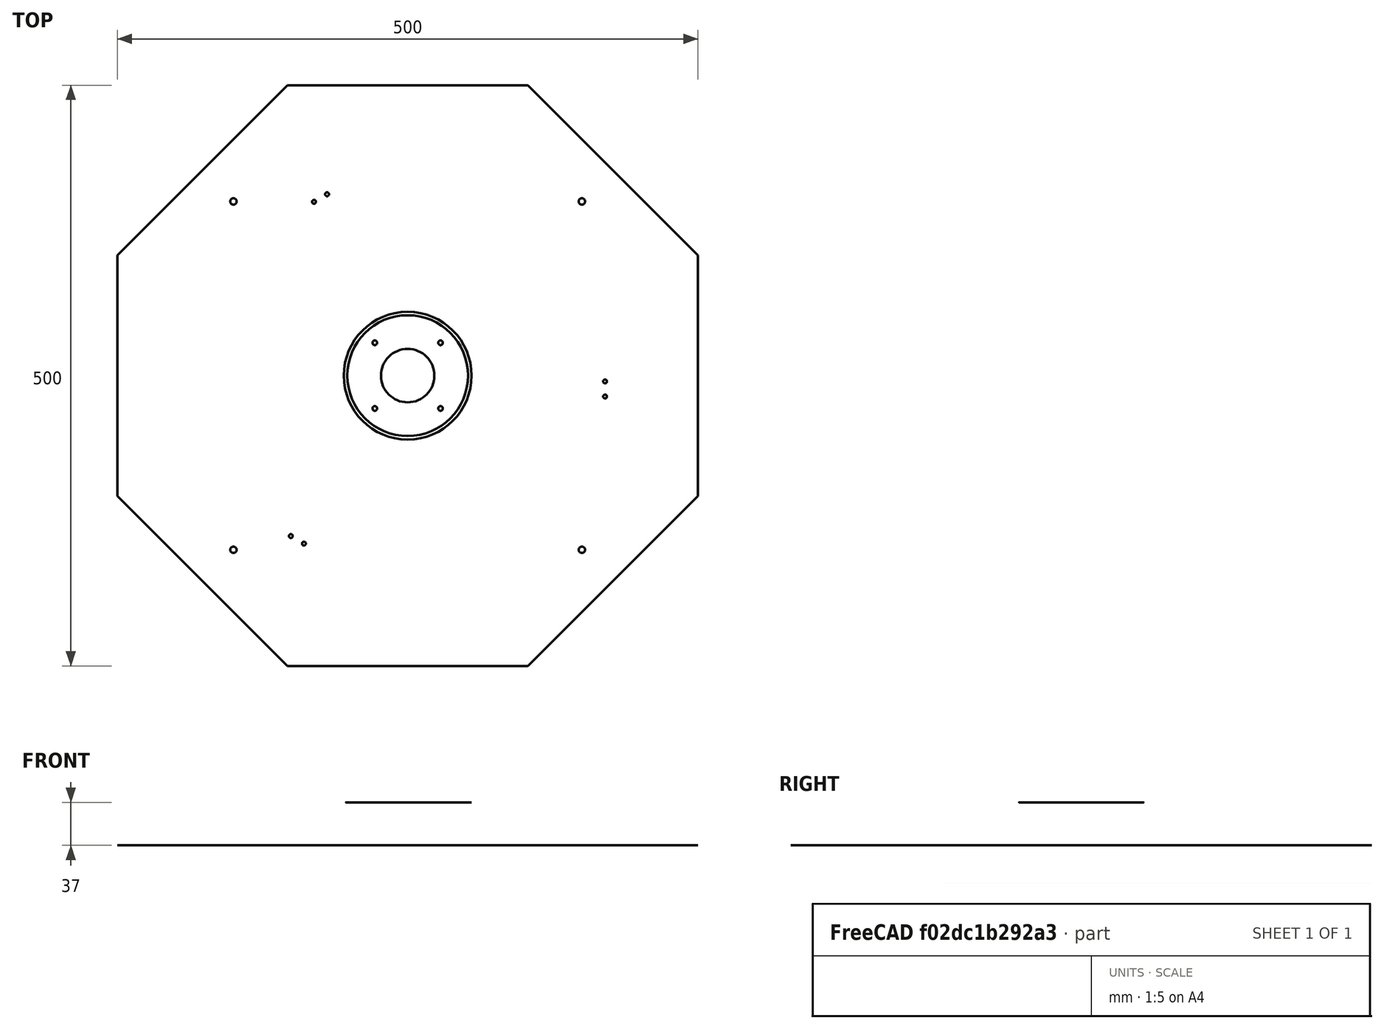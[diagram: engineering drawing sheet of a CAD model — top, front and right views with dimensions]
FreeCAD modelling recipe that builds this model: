
FCSTD DOCUMENT  (FreeCAD 0.19R24276 (Git))
Label: Baugruppe_Lampe_4er
License: All rights reserved
LicenseURL: http://en.wikipedia.org/wiki/All_rights_reserved
objects: Part::FeaturePython×25, App::Link×10, App::FeaturePython×5
note: 24 computed .brp shape members not serialized (recipe doc carries the construction recipe); baked Part::Feature solids carry a one-line shape summary decoded from their .brp
EXTERNAL_REF file=Metalicht_v2.FCStd obj=Body
EXTERNAL_REF file=Trichter.FCStd obj=Body
EXTERNAL_REF file=Birne_mit_Fassung.FCStd obj=Body
EXTERNAL_REF file=Wago_5x_flach.FCStd obj=Part__Feature

FEATURE [App::Link] Link  label="Body"
  LinkedObject = -> <external Metalicht_v2.FCStd>#Body
FEATURE [App::Link] Link001  label="Body001"
  LinkPlacement = pos=(0,0,1) rot=(0,0,1;0rad)
  LinkedObject = -> <external Trichter.FCStd>#Body
  Placement = pos=(0,0,1) rot=(0,0,1;0rad)
FEATURE [App::Link] Link002  label="Body002"
  LinkPlacement = pos=(164.77,44.4951,33.009) rot=(-0.043599,0.030528,-0.998583;4.36199rad)
  LinkedObject = -> <external Birne_mit_Fassung.FCStd>#Body
  Placement = pos=(164.77,44.4951,33.009) rot=(-0.043599,0.030528,-0.998583;4.36199rad)
FEATURE [App::Link] Link003  label="Body003"
  LinkPlacement = pos=(-44.668,164.613,33.009) rot=(0.043618,0.007691,0.999019;3.49032rad)
  LinkedObject = -> <external Birne_mit_Fassung.FCStd>#Body
  Placement = pos=(-44.668,164.613,33.009) rot=(0.043618,0.007691,0.999019;3.49032rad)
FEATURE [App::Link] Link004  label="Body004"
  LinkPlacement = pos=(44.4121,-164.782,33.0089) rot=(0.042343,-0.240138,0.969815;0.359701rad)
  LinkedObject = -> <external Birne_mit_Fassung.FCStd>#Body
  Placement = pos=(44.4121,-164.782,33.0089) rot=(0.042343,-0.240138,0.969815;0.359701rad)
FEATURE [App::Link] Link005  label="Wago_5x_flach"
  LinkPlacement = pos=(-69.5826,-37.87,-17.9525) rot=(0.57735,0.57735,-0.57735;4.18879rad)
  LinkedObject = -> <external Wago_5x_flach.FCStd>#Part__Feature
  Placement = pos=(-69.5826,-37.87,-17.9525) rot=(0.57735,0.57735,-0.57735;4.18879rad)
FEATURE [App::Link] Link006  label="Wago_5x_flach001"
  LinkPlacement = pos=(-69.5,59.5001,-18) rot=(0.57735,0.57735,-0.57735;4.18879rad)
  LinkedObject = -> <external Wago_5x_flach.FCStd>#Part__Feature
  Placement = pos=(-69.5,59.5001,-18) rot=(0.57735,0.57735,-0.57735;4.18879rad)
FEATURE [App::Link] Link007  label="Body005"
  LinkPlacement = pos=(-164.611,-44.4205,33.0759) rot=(-0.043535,-0.062174,-0.997115;1.22445rad)
  LinkedObject = -> <external Birne_mit_Fassung.FCStd>#Body
  Placement = pos=(-164.611,-44.4205,33.0759) rot=(-0.043535,-0.062174,-0.997115;1.22445rad)
FEATURE [App::Link] Link008  label="Wago_5x_flach002"
  LinkPlacement = pos=(69.5,-59.5001,-18) rot=(0.57735,-0.57735,0.57735;4.18879rad)
  LinkedObject = -> <external Wago_5x_flach.FCStd>#Part__Feature
  Placement = pos=(69.5,-59.5001,-18) rot=(0.57735,-0.57735,0.57735;4.18879rad)
FEATURE [App::Link] Link009  label="Wago_5x_flach003"
  LinkPlacement = pos=(69.546,37.646,-17.9) rot=(-0.57735,0.57735,-0.57735;2.0944rad)
  LinkedObject = -> <external Wago_5x_flach.FCStd>#Part__Feature
  Placement = pos=(69.546,37.646,-17.9) rot=(-0.57735,0.57735,-0.57735;2.0944rad)
FEATURE [Part::FeaturePython] Parts  # WARN: FeaturePython — macro-defined, semantics opaque (R4)
  Group = -> [Link,Link001,Link002,Link003,Link004,Link005,Link006,Link007,Link008,Link009]
  GroupMode = 0
FEATURE [Part::FeaturePython] Assembly  # WARN: FeaturePython — macro-defined, semantics opaque (R4)
  AutoRelax = true
  BuildShape = 0
  Freeze = false
  Group = -> [Constraints,Elements,Parts]
  Verbose = false
  _SolverType = 1
  _Version = 1
FEATURE [App::FeaturePython] Constraints  # WARN: FeaturePython — macro-defined, semantics opaque (R4)
  Group = -> [Constraint]
  _Version = 1
FEATURE [App::FeaturePython] Elements  # WARN: FeaturePython — macro-defined, semantics opaque (R4)
  Group = -> [_Element,_Element001,_Element002,_Element003,_Element004,_Element005,_Element006,_Element007,_Element008,_Element009,_Element010,_Element011,_Element012,_Element013,_Element014,_Element015,_Element016,_Element017,_Element018,_Element019,_Element020,_Element021,_Element022]
FEATURE [App::FeaturePython] Constraint  label="Locked"  # WARN: FeaturePython — macro-defined, semantics opaque (R4)
  Disabled = false
  Group = -> [ElementLink,ElementLink001]
  _ConstraintType = 0
  _Parent = -> Constraints
FEATURE [App::FeaturePython] ElementLink  label="_Element"  # link proxy (typed FeaturePython)
  LinkTransform = true
  LinkedObject = -> _Element
  _Parent = -> Constraint
FEATURE [Part::FeaturePython] _Element  # link proxy (typed FeaturePython)
  Detach = false
  LinkTransform = true
  LinkedObject = -> Link [PolarPattern.Face5]
  _Parent = -> Elements
FEATURE [App::FeaturePython] ElementLink001  label="_Element001"  # link proxy (typed FeaturePython)
  LinkTransform = true
  LinkedObject = -> _Element001
  _Parent = -> Constraint
FEATURE [Part::FeaturePython] _Element001  # link proxy (typed FeaturePython)
  Detach = false
  LinkTransform = true
  LinkedObject = -> Link001 [Revolution.Face2]
  _Parent = -> Elements
FEATURE [Part::FeaturePython] _Element002  # link proxy (typed FeaturePython)
  Detach = false
  LinkTransform = true
  LinkedObject = -> Link [PolarPattern.Edge37]
  _Parent = -> Elements
FEATURE [Part::FeaturePython] _Element003  # link proxy (typed FeaturePython)
  Detach = false
  LinkTransform = true
  LinkedObject = -> Link003 [Hole.Edge39]
  _Parent = -> Elements
FEATURE [Part::FeaturePython] _Element004  # link proxy (typed FeaturePython)
  Detach = false
  LinkTransform = true
  LinkedObject = -> Link [PolarPattern.Edge35]
  _Parent = -> Elements
FEATURE [Part::FeaturePython] _Element005  # link proxy (typed FeaturePython)
  Detach = false
  LinkTransform = true
  LinkedObject = -> Link003 [Hole.Edge38]
  _Parent = -> Elements
FEATURE [Part::FeaturePython] _Element006  # link proxy (typed FeaturePython)
  Detach = false
  LinkTransform = true
  LinkedObject = -> Link004 [Hole.Edge38]
  _Parent = -> Elements
FEATURE [Part::FeaturePython] _Element007  # link proxy (typed FeaturePython)
  Detach = false
  LinkTransform = true
  LinkedObject = -> Link [PolarPattern.Edge29]
  _Parent = -> Elements
FEATURE [Part::FeaturePython] _Element008  # link proxy (typed FeaturePython)
  Detach = false
  LinkTransform = true
  LinkedObject = -> Link [PolarPattern.Edge30]
  _Parent = -> Elements
FEATURE [Part::FeaturePython] _Element009  # link proxy (typed FeaturePython)
  Detach = false
  LinkTransform = true
  LinkedObject = -> Link004 [Hole.Edge39]
  _Parent = -> Elements
FEATURE [Part::FeaturePython] _Element010  # link proxy (typed FeaturePython)
  Detach = false
  LinkTransform = true
  LinkedObject = -> Link002 [Hole.Edge38]
  _Parent = -> Elements
FEATURE [Part::FeaturePython] _Element011  # link proxy (typed FeaturePython)
  Detach = false
  LinkTransform = true
  LinkedObject = -> Link [PolarPattern.Edge33]
  _Parent = -> Elements
FEATURE [Part::FeaturePython] _Element012  # link proxy (typed FeaturePython)
  Detach = false
  LinkTransform = true
  LinkedObject = -> Link [PolarPattern.Edge32]
  _Parent = -> Elements
FEATURE [Part::FeaturePython] _Element013  # link proxy (typed FeaturePython)
  Detach = false
  LinkTransform = true
  LinkedObject = -> Link002 [Hole.Edge39]
  _Parent = -> Elements
FEATURE [Part::FeaturePython] _Element014  # link proxy (typed FeaturePython)
  Detach = false
  LinkTransform = true
  LinkedObject = -> Link [PolarPattern.Edge36]
  _Parent = -> Elements
FEATURE [Part::FeaturePython] _Element015  # link proxy (typed FeaturePython)
  Detach = false
  LinkTransform = true
  LinkedObject = -> Link [PolarPattern.Edge34]
  _Parent = -> Elements
FEATURE [Part::FeaturePython] _Element016  # link proxy (typed FeaturePython)
  Detach = false
  LinkTransform = true
  LinkedObject = -> Link [Pocket002.Edge64]
  _Parent = -> Elements
FEATURE [Part::FeaturePython] _Element017  # link proxy (typed FeaturePython)
  Detach = false
  LinkTransform = true
  LinkedObject = -> Link [Pocket002.Edge63]
  _Parent = -> Elements
FEATURE [Part::FeaturePython] _Element018  # link proxy (typed FeaturePython)
  Detach = false
  LinkTransform = true
  LinkedObject = -> Link [Pocket002.Edge100]
  _Parent = -> Elements
FEATURE [Part::FeaturePython] _Element019  # link proxy (typed FeaturePython)
  Detach = false
  LinkTransform = true
  LinkedObject = -> Link [Pocket002.Edge99]
  _Parent = -> Elements
FEATURE [Part::FeaturePython] _Element020  # link proxy (typed FeaturePython)
  Detach = false
  LinkTransform = true
  LinkedObject = -> Link [Pocket002.Edge86]
  _Parent = -> Elements
FEATURE [Part::FeaturePython] _Element021  # link proxy (typed FeaturePython)
  Detach = false
  LinkTransform = true
  LinkedObject = -> Link [Pocket002.Edge88]
  _Parent = -> Elements
FEATURE [Part::FeaturePython] _Element022  # link proxy (typed FeaturePython)
  Detach = false
  LinkTransform = true
  LinkedObject = -> Link [Pocket002.Edge87]
  _Parent = -> Elements

RESOLVED EXTERNAL PARTS (link-assembly join: the EXTERNAL_REF files above that resolve inside this repo's crawl, each included once):
---- part Birne_mit_Fassung.FCStd = doc fcstd_91edc3af70b6 ----
FCSTD DOCUMENT  (FreeCAD 0.19R24276 (Git))
Label: Birne_mit_Fassung
License: All rights reserved
LicenseURL: http://en.wikipedia.org/wiki/All_rights_reserved
objects: Sketcher::SketchObject×3, PartDesign::Revolution×1, PartDesign::Pad×1, PartDesign::Fillet×1, PartDesign::Hole×1, PartDesign::Body×1
note: 12 computed .brp shape members not serialized (recipe doc carries the construction recipe); baked Part::Feature solids carry a one-line shape summary decoded from their .brp

FEATURE [Sketcher::SketchObject] Sketch
  FullyConstrained = true
  MapMode = 5
  Placement = pos=(0,0,0) rot=(1,0,0;1.5708rad)
  Support = -> [XZ_Plane]
  sketch-geometry (8):
    g0: LineSegment StartX=0 StartY=0 StartZ=0 EndX=0 EndY=17.5 EndZ=0
    g1: LineSegment StartX=0 StartY=17.5 StartZ=0 EndX=36 EndY=20 EndZ=0
    g2: LineSegment StartX=36 StartY=20 StartZ=0 EndX=36 EndY=21 EndZ=0
    g3: LineSegment StartX=36 StartY=21 StartZ=0 EndX=48 EndY=21 EndZ=0
    g4: LineSegment StartX=48 StartY=21 StartZ=0 EndX=48 EndY=17 EndZ=0
    g5: LineSegment StartX=48 StartY=17 StartZ=0 EndX=87 EndY=21.4243 EndZ=0
    g6: ArcOfCircle CenterX=108 CenterY=0 CenterZ=0 NormalX=0 NormalY=0 NormalZ=1 AngleXU=0 Radius=30 StartAngle=0 EndAngle=2.34619
    g7: LineSegment StartX=138 StartY=0 StartZ=0 EndX=0 EndY=0 EndZ=0
  constraints (24):
    c: Coincident(g-1,g0)
    c: PointOnObject(g0,g-2)
    c: Coincident(g0,g1)
    c: Coincident(g1,g2)
    c: Vertical(g2)
    c: Coincident(g2,g3)
    c: Horizontal(g3)
    c: Coincident(g3,g4)
    c: Vertical(g4)
    c: Coincident(g4,g5)
    c: PointOnObject(g6,g-1)
    c: Coincident(g6,g5)
    c: PointOnObject(g6,g-1)
    c: Coincident(g7,g6)
    c: Coincident(g7,g0)
    c: DistanceX(g0,g3) = 48
    c: Radius(g6) = 30
    c: DistanceX(g4,g6) = 90
    c: DistanceX(g3,g3) = 12
    c: DistanceX(g4,g5) = 39
    c: DistanceY(g0,g0) = 17.5
    c: DistanceY(g0,g3) = 21
    c: DistanceY(g2,g2) = 1
    c: DistanceY(g0,g4) = 17
FEATURE [PartDesign::Revolution] Revolution
  Angle = 360
  Axis = (1,0,0)
  Base = (0,0,0)
  Placement = pos=(0,0,0) rot=(1,0,0;1.5708rad)
  Profile = -> Sketch
  ReferenceAxis = -> Sketch [H_Axis]
FEATURE [Sketcher::SketchObject] Sketch001
  FullyConstrained = true
  MapMode = 5
  Placement = pos=(0,0,0) rot=(1,0,0;1.5708rad)
  Support = -> [XZ_Plane]
  sketch-geometry (6):
    g0: LineSegment StartX=0 StartY=0 StartZ=0 EndX=0 EndY=-30.6255 EndZ=0
    g1: LineSegment StartX=0 StartY=-30.6255 StartZ=0 EndX=21.5432 EndY=-32.5103 EndZ=0
    g2: LineSegment StartX=21.5432 StartY=-32.5103 StartZ=0 EndX=21.4125 EndY=-34.0046 EndZ=0
    g3: LineSegment StartX=21.4125 StartY=-34.0046 StartZ=0 EndX=-1.5 EndY=-32 EndZ=0
    g4: LineSegment StartX=-1.5 StartY=-32 StartZ=0 EndX=-1.5 EndY=0 EndZ=0
    g5: LineSegment StartX=-1.5 StartY=0 StartZ=0 EndX=0 EndY=0 EndZ=0
  constraints (17):
    c: Coincident(g-1,g0)
    c: PointOnObject(g0,g-2)
    c: Coincident(g0,g1)
    c: Coincident(g1,g2)
    c: Coincident(g2,g3)
    c: Coincident(g3,g4)
    c: PointOnObject(g4,g-1)
    c: Vertical(g4)
    c: Coincident(g4,g5)
    c: Coincident(g5,g0)
    c: Perpendicular(g2,g3)
    c: Perpendicular(g1,g2)
    c: Equal(g5,g2)
    c: DistanceX(g5,g5) = 1.5
    c: DistanceY(g4,g4) = 32
    c: Angle(g1,g0) = 1.65806
    c: Distance(g3) = 23
FEATURE [PartDesign::Pad] Pad
  BaseFeature = -> Revolution
  Direction = (1,1,1)
  Length = 8
  Length2 = 100
  Midplane = true
  Placement = pos=(0,0,0) rot=(1,0,0;1.5708rad)
  Profile = -> Sketch001
  Type = 0
FEATURE [PartDesign::Fillet] Fillet
  Base = -> Pad [Edge30]
  BaseFeature = -> Pad
  Placement = pos=(0,0,0) rot=(1,0,0;1.5708rad)
  Radius = 25
  SupportTransform = false
FEATURE [Sketcher::SketchObject] Sketch002
  FullyConstrained = false
  MapMode = 5
  Placement = pos=(-2.78977,-2.12e-14,-31.8872) rot=(0.999048,0,-0.043619;3.14159rad)
  Support = -> [Fillet]
  sketch-geometry (2):
    g0: Circle CenterX=8 CenterY=0 CenterZ=0 NormalX=0 NormalY=0 NormalZ=1 AngleXU=0 Radius=2.06982
    g1: Circle CenterX=21 CenterY=0 CenterZ=0 NormalX=0 NormalY=0 NormalZ=1 AngleXU=0 Radius=2.01033
  constraints (4):
    c: PointOnObject(g0,g-1)
    c: PointOnObject(g1,g-1)
    c: DistanceX(g0,g1) = 13
    c: DistanceX(g-1,g0) = 8
FEATURE [PartDesign::Hole] Hole
  BaseFeature = -> Fillet
  Depth = 3
  DepthType = 0
  Diameter = 2.5
  DrillForDepth = false
  DrillPoint = 1
  DrillPointAngle = 118
  HoleCutCountersinkAngle = 90
  HoleCutCustomValues = false
  HoleCutDepth = 0
  HoleCutDiameter = 6.1
  HoleCutType = 0
  ModelActualThread = false
  Placement = pos=(0,0,0) rot=(1,0,0;1.5708rad)
  Profile = -> Sketch002
  Tapered = false
  TaperedAngle = 90
  ThreadAngle = 60
  ThreadClass = 5
  ThreadCutOffInner = 0.0541266
  ThreadCutOffOuter = 0.108253
  ThreadDirection = 0
  ThreadFit = 0
  ThreadPitch = 0.5
  ThreadSize = 9
  ThreadType = 1
  Threaded = true
FEATURE [PartDesign::Body] Body
  Group = -> [Sketch,Revolution,Sketch001,Pad,Fillet,Sketch002,Hole]
  Origin = -> Origin
  Tip = -> Hole
---- part Metalicht_v2.FCStd = doc fcstd_c46f964f9d03 ----
FCSTD DOCUMENT  (FreeCAD 0.19R24276 (Git))
Label: Metalicht_v2
License: All rights reserved
LicenseURL: http://en.wikipedia.org/wiki/All_rights_reserved
objects: Sketcher::SketchObject×7, PartDesign::Pocket×6, PartDesign::PolarPattern×2, PartDesign::Pad×1, PartDesign::Fillet×1, PartDesign::Body×1
note: 26 computed .brp shape members not serialized (recipe doc carries the construction recipe); baked Part::Feature solids carry a one-line shape summary decoded from their .brp

FEATURE [Sketcher::SketchObject] Sketch
  FullyConstrained = true
  MapMode = 5
  Support = -> [XY_Plane]
  sketch-geometry (21):
    g0: Circle CenterX=0 CenterY=0 CenterZ=0 NormalX=0 NormalY=0 NormalZ=1 AngleXU=0 Radius=250
    g1: Circle CenterX=0 CenterY=0 CenterZ=0 NormalX=0 NormalY=0 NormalZ=1 AngleXU=0 Radius=23
    g2: Circle CenterX=150 CenterY=150 CenterZ=0 NormalX=0 NormalY=0 NormalZ=1 AngleXU=0 Radius=2.75
    g3: Circle CenterX=-150 CenterY=150 CenterZ=0 NormalX=0 NormalY=0 NormalZ=1 AngleXU=0 Radius=2.75
    g4: Circle CenterX=-150 CenterY=-150 CenterZ=0 NormalX=0 NormalY=0 NormalZ=1 AngleXU=0 Radius=2.75
    g5: Circle CenterX=150 CenterY=-150 CenterZ=0 NormalX=0 NormalY=0 NormalZ=1 AngleXU=0 Radius=2.75
    g6: LineSegment StartX=103.553 StartY=250 StartZ=0 EndX=-103.553 EndY=250 EndZ=0
    g7: LineSegment StartX=-103.553 StartY=250 StartZ=0 EndX=-250 EndY=103.553 EndZ=0
    g8: LineSegment StartX=-250 StartY=103.553 StartZ=0 EndX=-250 EndY=-103.553 EndZ=0
    g9: LineSegment StartX=-250 StartY=-103.553 StartZ=0 EndX=-103.553 EndY=-250 EndZ=0
    g10: LineSegment StartX=-103.553 StartY=-250 StartZ=0 EndX=103.553 EndY=-250 EndZ=0
    g11: LineSegment StartX=103.553 StartY=-250 StartZ=0 EndX=250 EndY=-103.553 EndZ=0
    g12: LineSegment StartX=250 StartY=-103.553 StartZ=0 EndX=250 EndY=103.553 EndZ=0
    g13: LineSegment StartX=250 StartY=103.553 StartZ=0 EndX=103.553 EndY=250 EndZ=0
    g14: Circle CenterX=0 CenterY=0 CenterZ=0 NormalX=0 NormalY=0 NormalZ=1 AngleXU=0 Radius=270.598
    g15: Circle CenterX=28.2843 CenterY=28.2843 CenterZ=0 NormalX=0 NormalY=0 NormalZ=1 AngleXU=0 Radius=2
    g16: Circle CenterX=-28.2843 CenterY=28.2843 CenterZ=0 NormalX=0 NormalY=0 NormalZ=1 AngleXU=0 Radius=2
    g17: Circle CenterX=-28.2843 CenterY=-28.2843 CenterZ=0 NormalX=0 NormalY=0 NormalZ=1 AngleXU=0 Radius=2
    g18: Circle CenterX=28.2843 CenterY=-28.2843 CenterZ=0 NormalX=0 NormalY=0 NormalZ=1 AngleXU=0 Radius=2
    g19: LineSegment StartX=-28.2843 StartY=28.2843 StartZ=0 EndX=28.2843 EndY=28.2843 EndZ=0
    g20: LineSegment StartX=-28.2843 StartY=28.2843 StartZ=0 EndX=-28.2843 EndY=-28.2843 EndZ=0
  constraints (46):
    c: Coincident(g0,g-1)
    c: Diameter(g0) = 500
    c: Coincident(g1,g0)
    c: Diameter(g1) = 46
    c: Equal(g5,g4)
    c: Equal(g4,g3)
    c: Equal(g3,g2)
    c: Diameter(g2) = 5.5
    c: Symmetric(g2,g5,g-1)
    c: Symmetric(g5,g4,g-2)
    c: Symmetric(g3,g2,g-2)
    c: DistanceX(g3,g2) = 300
    c: DistanceY(g5,g2) = 300
    c: Coincident(g6,g7)
    c: Coincident(g7,g8)
    c: Coincident(g8,g9)
    c: Coincident(g9,g10)
    c: Coincident(g10,g11)
    c: Coincident(g11,g12)
    c: Coincident(g12,g13)
    c: Coincident(g13,g6)
    c: Equal(g6, g7-g13) x7
    c: PointOnObject(g6,g14)
    c: PointOnObject(g7,g14)
    c: PointOnObject(g8,g14)
    c: PointOnObject(g9,g14)
    c: PointOnObject(g10,g14)
    c: PointOnObject(g11,g14)
    c: PointOnObject(g12,g14)
    c: PointOnObject(g13,g14)
    c: Coincident(g14,g1)
    c: Tangent(g0,g6)
    c: Horizontal(g6)
    c: Symmetric(g16,g15,g-2)
    c: Symmetric(g17,g16,g-1)
    c: Symmetric(g17,g18,g-2)
    c: Equal(g16,g17)
    c: Equal(g17,g18)
    c: Equal(g18,g15)
    c: Distance(g16,g1) = 40
    c: Coincident(g19,g16)
    c: Coincident(g19,g15)
    c: Coincident(g20,g16)
    c: Coincident(g20,g17)
    c: Equal(g20,g19)
    c: Diameter(g16) = 4
FEATURE [PartDesign::Pad] Pad
  Direction = (1,1,1)
  Length = 1
  Length2 = 100
  Profile = -> Sketch
  Type = 0
FEATURE [Sketcher::SketchObject] Sketch001
  FullyConstrained = true
  MapMode = 5
  Support = -> [XY_Plane]
  sketch-geometry (3):
    g0: Circle CenterX=169.926 CenterY=-5 CenterZ=0 NormalX=0 NormalY=0 NormalZ=1 AngleXU=0 Radius=1.65
    g1: Circle CenterX=169.926 CenterY=-18 CenterZ=0 NormalX=0 NormalY=0 NormalZ=1 AngleXU=0 Radius=1.65
    g2: LineSegment StartX=169.926 StartY=-5 StartZ=0 EndX=169.926 EndY=-18 EndZ=0
  constraints (8):
    c: Equal(g1,g0)
    c: Diameter(g0) = 3.3
    c: Distance(g1,g0) = 13
    c: Coincident(g2,g0)
    c: Coincident(g2,g1)
    c: Angle(g-1,g2) = 1.5708
    c: DistanceY(g0,g-1) = 5
    c: Distance(g-1,g0) = 170
FEATURE [PartDesign::Pocket] Pocket
  BaseFeature = -> Pad
  Length = 5
  Length2 = 100
  Profile = -> Sketch001
  Reversed = true
  Type = 1
FEATURE [PartDesign::PolarPattern] PolarPattern
  Angle = 360
  Axis = -> Sketch001 [N_Axis]
  BaseFeature = -> Pocket
  Occurrences = 3
  Originals = -> [Pocket]
FEATURE [Sketcher::SketchObject] Sketch002
  FullyConstrained = true
  MapMode = 5
  Support = -> [XY_Plane]
  sketch-geometry (4):
    g0: ArcOfCircle CenterX=-60 CenterY=0 CenterZ=0 NormalX=0 NormalY=0 NormalZ=1 AngleXU=0 Radius=8 StartAngle=1.5708 EndAngle=4.71239
    g1: ArcOfCircle CenterX=60 CenterY=0 CenterZ=0 NormalX=0 NormalY=0 NormalZ=1 AngleXU=0 Radius=8 StartAngle=4.71239 EndAngle=7.85398
    g2: LineSegment StartX=-60 StartY=-8 StartZ=0 EndX=60 EndY=-8 EndZ=0
    g3: LineSegment StartX=-60 StartY=8 StartZ=0 EndX=60 EndY=8 EndZ=0
  constraints (9):
    c: Tangent(g0,g3) = 1.5708
    c: Tangent(g0,g2) = -1.5708
    c: Tangent(g2,g1) = -1.5708
    c: Tangent(g3,g1) = 1.5708
    c: Horizontal(g2)
    c: PointOnObject(g0,g-1)
    c: Symmetric(g0,g1,g-2)
    c: Radius(g1) = 8
    c: DistanceX(g3,g3) = 120
FEATURE [PartDesign::Pocket] Pocket001
  BaseFeature = -> PolarPattern
  Length = 5
  Length2 = 100
  Profile = -> Sketch002
  Reversed = true
  Type = 0
FEATURE [Sketcher::SketchObject] Sketch003
  FullyConstrained = true
  MapMode = 5
  Support = -> [XY_Plane]
  sketch-geometry (42):
    g0: Circle CenterX=-80 CenterY=71 CenterZ=0 NormalX=0 NormalY=0 NormalZ=1 AngleXU=0 Radius=1.1
    g1: Circle CenterX=-80 CenterY=26 CenterZ=0 NormalX=0 NormalY=0 NormalZ=1 AngleXU=0 Radius=1.1
    g2: Circle CenterX=-80 CenterY=-26 CenterZ=0 NormalX=0 NormalY=0 NormalZ=1 AngleXU=0 Radius=1.1
    g3: Circle CenterX=-80 CenterY=-71 CenterZ=0 NormalX=0 NormalY=0 NormalZ=1 AngleXU=0 Radius=1.1
    g4: Circle CenterX=-80 CenterY=0 CenterZ=0 NormalX=0 NormalY=0 NormalZ=1 AngleXU=0 Radius=1.45
    g5: LineSegment StartX=-95 StartY=51 StartZ=0 EndX=-105 EndY=51 EndZ=0
    g6: LineSegment StartX=-105 StartY=51 StartZ=0 EndX=-105 EndY=45 EndZ=0
    g7: LineSegment StartX=-105 StartY=45 StartZ=0 EndX=-103.5 EndY=45 EndZ=0
    g8: LineSegment StartX=-103.5 StartY=45 StartZ=0 EndX=-103.5 EndY=49.5 EndZ=0
    g9: LineSegment StartX=-103.5 StartY=49.5 StartZ=0 EndX=-95 EndY=49.5 EndZ=0
    g10: LineSegment StartX=-95 StartY=49.5 StartZ=0 EndX=-95 EndY=51 EndZ=0
    g11: LineSegment StartX=-105 StartY=-45 StartZ=0 EndX=-95 EndY=-45 EndZ=0
    g12: LineSegment StartX=-95 StartY=-45 StartZ=0 EndX=-101.312 EndY=-49.5 EndZ=0
    g13: LineSegment StartX=-101.312 StartY=-49.5 StartZ=0 EndX=-96 EndY=-49.5 EndZ=0
    g14: LineSegment StartX=-96 StartY=-49.5 StartZ=0 EndX=-96 EndY=-51 EndZ=0
    g15: LineSegment StartX=-96 StartY=-51 StartZ=0 EndX=-106 EndY=-51 EndZ=0
    g16: LineSegment StartX=-106 StartY=-51 StartZ=0 EndX=-99.688 EndY=-46.5 EndZ=0
    g17: LineSegment StartX=-99.688 StartY=-46.5 StartZ=0 EndX=-105 EndY=-46.5 EndZ=0
    g18: LineSegment StartX=-105 StartY=-46.5 StartZ=0 EndX=-105 EndY=-45 EndZ=0
    g19: LineSegment StartX=-99.688 StartY=-46.5 StartZ=0 EndX=-98.8172 EndY=-47.7214 EndZ=0
    g20: LineSegment StartX=-105 StartY=-45 StartZ=0 EndX=-105 EndY=45 EndZ=0
    g21: Circle CenterX=80 CenterY=71 CenterZ=0 NormalX=0 NormalY=0 NormalZ=1 AngleXU=0 Radius=1.1
    g22: Circle CenterX=80 CenterY=26 CenterZ=0 NormalX=0 NormalY=0 NormalZ=1 AngleXU=0 Radius=1.1
    g23: Circle CenterX=80 CenterY=0 CenterZ=0 NormalX=0 NormalY=0 NormalZ=1 AngleXU=0 Radius=1.45
    g24: Circle CenterX=80 CenterY=-26 CenterZ=0 NormalX=0 NormalY=0 NormalZ=1 AngleXU=0 Radius=1.1
    g25: Circle CenterX=80 CenterY=-71 CenterZ=0 NormalX=0 NormalY=0 NormalZ=1 AngleXU=0 Radius=1.1
    g26: LineSegment StartX=105 StartY=-51 StartZ=0 EndX=95 EndY=-51 EndZ=0
    g27: LineSegment StartX=95 StartY=-51 StartZ=0 EndX=101.312 EndY=-46.5 EndZ=0
    g28: LineSegment StartX=101.312 StartY=-46.5 StartZ=0 EndX=96 EndY=-46.5 EndZ=0
    g29: LineSegment StartX=96 StartY=-46.5 StartZ=0 EndX=96 EndY=-45 EndZ=0
    g30: LineSegment StartX=96 StartY=-45 StartZ=0 EndX=106 EndY=-45 EndZ=0
    g31: LineSegment StartX=106 StartY=-45 StartZ=0 EndX=99.688 EndY=-49.5 EndZ=0
    g32: LineSegment StartX=99.688 StartY=-49.5 StartZ=0 EndX=105 EndY=-49.5 EndZ=0
    g33: LineSegment StartX=105 StartY=-49.5 StartZ=0 EndX=105 EndY=-51 EndZ=0
    g34: LineSegment StartX=99.688 StartY=-49.5 StartZ=0 EndX=98.8172 EndY=-48.2786 EndZ=0
    g35: LineSegment StartX=95 StartY=45 StartZ=0 EndX=105 EndY=45 EndZ=0
    g36: LineSegment StartX=105 StartY=45 StartZ=0 EndX=105 EndY=51 EndZ=0
    g37: LineSegment StartX=105 StartY=51 StartZ=0 EndX=103.5 EndY=51 EndZ=0
    g38: LineSegment StartX=103.5 StartY=51 StartZ=0 EndX=103.5 EndY=46.5 EndZ=0
    g39: LineSegment StartX=103.5 StartY=46.5 StartZ=0 EndX=95 EndY=46.5 EndZ=0
    g40: LineSegment StartX=95 StartY=46.5 StartZ=0 EndX=95 EndY=45 EndZ=0
    g41: LineSegment StartX=105 StartY=45 StartZ=0 EndX=105 EndY=-45 EndZ=0
  constraints (116):
    c: Equal(g3,g2)
    c: Equal(g2,g1)
    c: Equal(g1,g0)
    c: Vertical(g0,g1)
    c: Symmetric(g0,g3,g-1)
    c: Symmetric(g1,g2,g-1)
    c: DistanceY(g1,g0) = 45
    c: DistanceY(g-1,g1) = 26
    c: Diameter(g0) = 2.2
    c: DistanceX(g1,g-1) = 80
    c: PointOnObject(g4,g-1)
    c: Vertical(g1,g4)
    c: Diameter(g4) = 2.9
    c: Coincident(g5,g6)
    c: Coincident(g6,g7)
    c: Horizontal(g7)
    c: Coincident(g7,g8)
    c: Vertical(g8)
    c: Coincident(g8,g9)
    c: Horizontal(g9)
    c: Coincident(g9,g10)
    c: Coincident(g10,g5)
    c: Vertical(g10)
    c: Horizontal(g11)
    c: Coincident(g11,g12)
    c: Coincident(g12,g13)
    c: Coincident(g13,g14)
    c: Vertical(g14)
    c: Coincident(g14,g15)
    c: Horizontal(g15)
    c: Coincident(g15,g16)
    c: Coincident(g16,g17)
    c: Coincident(g17,g18)
    c: Coincident(g18,g11)
    c: Vertical(g18)
    c: Horizontal(g13)
    c: Horizontal(g17)
    c: Parallel(g16,g12)
    c: Coincident(g19,g16)
    c: Coincident(g20,g11)
    c: Coincident(g20,g6)
    c: Perpendicular(g19,g16)
    c: Equal(g19,g14)
    c: DistanceY(g14,g14) = 1.5
    c: DistanceX(g13,g11) = 1
    c: DistanceX(g15,g17) = 1
    c: DistanceX(g11,g11) = 10
    c: Vertical(g6)
    c: Horizontal(g5)
    c: Equal(g10,g14)
    c: DistanceY(g6,g6) = 6
    c: DistanceX(g5,g5) = 10
    c: Symmetric(g6,g11,g-1)
    c: DistanceY(g20,g20) = 90
    c: DistanceX(g17,g2) = 25
    c: PointOnObject(g19,g12)
    c: Equal(g18,g19)
    c: DistanceY(g14,g11) = 6
    c: Equal(g25,g24)
    c: Equal(g24,g22)
    c: Equal(g22,g21)
    c: Equal(g25,g3)
    c: Symmetric(g3,g25,g-2)
    c: Symmetric(g2,g24,g-2)
    c: Symmetric(g22,g1,g-2)
    c: Symmetric(g0,g21,g-2)
    c: Symmetric(g23,g4,g-2)
    c: Equal(g4,g23)
    c: Equal(g7,g10)
    c: Horizontal(g26)
    c: Coincident(g26,g27)
    c: Coincident(g27,g28)
    c: Horizontal(g28)
    c: Coincident(g28,g29)
    c: Vertical(g29)
    c: Coincident(g29,g30)
    c: Horizontal(g30)
    c: Coincident(g30,g31)
    c: Coincident(g31,g32)
    c: Horizontal(g32)
    c: Coincident(g32,g33)
    c: Coincident(g33,g26)
    c: Vertical(g33)
    c: Coincident(g34,g31)
    c: PointOnObject(g34,g27)
    c: Perpendicular(g27,g34)
    c: Parallel(g31,g27)
    c: Equal(g33,g29)
    c: Equal(g29,g34)
    c: Horizontal(g35)
    c: Coincident(g35,g36)
    c: Vertical(g36)
    c: Coincident(g36,g37)
    c: Horizontal(g37)
    c: Coincident(g37,g38)
    c: Vertical(g38)
    c: Coincident(g38,g39)
    c: Horizontal(g39)
    c: Coincident(g39,g40)
    c: Coincident(g40,g35)
    c: Vertical(g40)
    c: Coincident(g41,g35)
    c: PointOnObject(g41,g30)
    c: Vertical(g41)
    c: Symmetric(g35,g6,g-2)
    c: Equal(g9,g39)
    c: Equal(g37,g40)
    c: Equal(g40,g7)
    c: Equal(g36,g6)
    c: PointOnObject(g32,g41)
    c: Equal(g30,g15)
    c: Parallel(g27,g16)
    c: Equal(g41,g20)
    c: Equal(g29,g19)
    c: Equal(g31,g12)
    c: Equal(g28,g32)
FEATURE [PartDesign::Pocket] Pocket002
  BaseFeature = -> Pocket001
  Length = 5
  Length2 = 100
  Profile = -> Sketch003
  Reversed = true
  Type = 1
FEATURE [Sketcher::SketchObject] Sketch004
  FullyConstrained = true
  MapMode = 5
  Support = -> [XY_Plane]
  sketch-geometry (6):
    g0: Circle CenterX=-32.5 CenterY=-56.2917 CenterZ=0 NormalX=0 NormalY=0 NormalZ=1 AngleXU=0 Radius=1.45
    g1: Circle CenterX=32.5 CenterY=-56.2917 CenterZ=0 NormalX=0 NormalY=0 NormalZ=1 AngleXU=0 Radius=1.45
    g2: Circle CenterX=-32.5 CenterY=56.2917 CenterZ=0 NormalX=0 NormalY=0 NormalZ=1 AngleXU=0 Radius=1.45
    g3: Circle CenterX=32.5 CenterY=56.2917 CenterZ=0 NormalX=0 NormalY=0 NormalZ=1 AngleXU=0 Radius=1.45
    g4: Circle CenterX=0 CenterY=0 CenterZ=0 NormalX=0 NormalY=0 NormalZ=1 AngleXU=0 Radius=65
    g5: LineSegment StartX=0 StartY=0 StartZ=0 EndX=32.5 EndY=56.2917 EndZ=0
  constraints (13):
    c: Coincident(g4,g-1)
    c: PointOnObject(g3,g4)
    c: Radius(g4) = 65
    c: Equal(g2,g0)
    c: Equal(g0,g1)
    c: Equal(g1,g3)
    c: Symmetric(g2,g3,g-2)
    c: Symmetric(g0,g1,g-2)
    c: Symmetric(g1,g3,g-1)
    c: Coincident(g5,g-1)
    c: Coincident(g5,g3)
    c: Angle(g5,g-2) = 0.523599
    c: Diameter(g3) = 2.9
FEATURE [PartDesign::Pocket] Pocket003
  BaseFeature = -> Pocket002
  Length = 5
  Length2 = 100
  Profile = -> Sketch004
  Reversed = true
  Type = 1
FEATURE [Sketcher::SketchObject] Sketch005
  FullyConstrained = true
  MapMode = 5
  Support = -> [XY_Plane]
  sketch-geometry (10):
    g0: Circle CenterX=135 CenterY=150 CenterZ=0 NormalX=0 NormalY=0 NormalZ=1 AngleXU=0 Radius=2.1
    g1: Circle CenterX=165 CenterY=150 CenterZ=0 NormalX=0 NormalY=0 NormalZ=1 AngleXU=0 Radius=2.1
    g2: LineSegment StartX=0 StartY=0 StartZ=0 EndX=150 EndY=150 EndZ=0
    g3: Circle CenterX=-165 CenterY=150 CenterZ=0 NormalX=0 NormalY=0 NormalZ=1 AngleXU=0 Radius=2.1
    g4: Circle CenterX=-135 CenterY=150 CenterZ=0 NormalX=0 NormalY=0 NormalZ=1 AngleXU=0 Radius=2.1
    g5: Circle CenterX=-165 CenterY=-150 CenterZ=0 NormalX=0 NormalY=0 NormalZ=1 AngleXU=0 Radius=2.1
    g6: Circle CenterX=-135 CenterY=-150 CenterZ=0 NormalX=0 NormalY=0 NormalZ=1 AngleXU=0 Radius=2.1
    g7: Circle CenterX=135 CenterY=-150 CenterZ=0 NormalX=0 NormalY=0 NormalZ=1 AngleXU=0 Radius=2.1
    g8: Circle CenterX=165 CenterY=-150 CenterZ=0 NormalX=0 NormalY=0 NormalZ=1 AngleXU=0 Radius=2.1
    g9: LineSegment StartX=150 StartY=150 StartZ=0 EndX=150 EndY=0 EndZ=0
  constraints (23):
    c: Horizontal(g0,g1)
    c: Coincident(g2,g-1)
    c: Equal(g7,g6)
    c: Equal(g6,g5)
    c: Equal(g5,g8)
    c: Equal(g8,g3)
    c: Equal(g3,g4)
    c: Equal(g4,g0)
    c: Equal(g0,g1)
    c: Horizontal(g2,g1)
    c: DistanceX(g2,g2) = 150
    c: DistanceY(g2,g2) = 150
    c: Coincident(g9,g2)
    c: PointOnObject(g9,g-1)
    c: Symmetric(g0,g1,g9)
    c: DistanceX(g0,g1) = 30
    c: Diameter(g1) = 4.2
    c: Symmetric(g0,g4,g-2)
    c: Symmetric(g3,g1,g-2)
    c: Symmetric(g0,g7,g-1)
    c: Symmetric(g1,g8,g-1)
    c: Symmetric(g5,g8,g-2)
    c: Symmetric(g6,g7,g-2)
FEATURE [PartDesign::Pocket] Pocket004
  BaseFeature = -> Pocket003
  Length = 5
  Length2 = 100
  Profile = -> Sketch005
  Reversed = true
  Type = 1
FEATURE [Sketcher::SketchObject] Sketch006
  FullyConstrained = true
  MapMode = 5
  Support = -> [XY_Plane]
  sketch-geometry (4):
    g0: LineSegment StartX=0 StartY=0 StartZ=0 EndX=-159.748 EndY=-58.1434 EndZ=0
    g1: Circle CenterX=-161.971 CenterY=-52.0354 CenterZ=0 NormalX=0 NormalY=0 NormalZ=1 AngleXU=0 Radius=1.65
    g2: Circle CenterX=-157.525 CenterY=-64.2514 CenterZ=0 NormalX=0 NormalY=0 NormalZ=1 AngleXU=0 Radius=1.65
    g3: LineSegment StartX=-161.971 StartY=-52.0354 StartZ=0 EndX=-157.525 EndY=-64.2514 EndZ=0
  constraints (10):
    c: Coincident(g0,g-1)
    c: Distance(g0) = 170
    c: Angle(g0,g-1) = 2.79253
    c: Symmetric(g1,g2,g0)
    c: Equal(g1,g2)
    c: Coincident(g3,g1)
    c: Coincident(g3,g2)
    c: PointOnObject(g0,g3)
    c: Diameter(g1) = 3.3
    c: Distance(g3) = 13
FEATURE [PartDesign::Pocket] Pocket005
  BaseFeature = -> Pocket004
  Length = 5
  Length2 = 100
  Profile = -> Sketch006
  Reversed = true
  Type = 1
FEATURE [PartDesign::PolarPattern] PolarPattern001
  Angle = 360
  Axis = -> Sketch006 [N_Axis]
  BaseFeature = -> Pocket005
  Occurrences = 4
  Originals = -> [Pocket005]
FEATURE [PartDesign::Fillet] Fillet
  Base = -> PolarPattern001 [Edge182,Edge184,Edge183,Edge8,Edge2,Edge1,Edge5,Edge181]
  BaseFeature = -> PolarPattern001
  Radius = 15
  SupportTransform = false
FEATURE [PartDesign::Body] Body
  Group = -> [Sketch,Pad,Sketch001,Pocket,PolarPattern,Sketch002,Pocket001,Sketch003,Pocket002,Sketch004,Pocket003,Sketch005,Pocket004,Sketch006,Pocket005,PolarPattern001,Fillet]
  Origin = -> Origin
  Tip = -> Fillet
---- part Trichter.FCStd = doc fcstd_8d90fd25db23 ----
FCSTD DOCUMENT  (FreeCAD 0.19R24276 (Git))
Label: Trichter
License: All rights reserved
LicenseURL: http://en.wikipedia.org/wiki/All_rights_reserved
objects: Sketcher::SketchObject×6, PartDesign::PolarPattern×4, PartDesign::Pocket×3, PartDesign::Plane×2, PartDesign::Pad×2, PartDesign::Revolution×1, PartDesign::Fillet×1, PartDesign::Body×1
note: 27 computed .brp shape members not serialized (recipe doc carries the construction recipe); baked Part::Feature solids carry a one-line shape summary decoded from their .brp

FEATURE [Sketcher::SketchObject] Sketch
  FullyConstrained = true
  MapMode = 5
  Placement = pos=(0,0,0) rot=(1,0,0;1.5708rad)
  Support = -> [XZ_Plane]
  sketch-geometry (9):
    g0: LineSegment StartX=20 StartY=0 StartZ=0 EndX=20 EndY=5 EndZ=0
    g1: LineSegment StartX=55 StartY=37 StartZ=0 EndX=55 EndY=0 EndZ=0
    g2: LineSegment StartX=55 StartY=0 StartZ=0 EndX=20 EndY=0 EndZ=0
    g3: LineSegment StartX=20 StartY=5 StartZ=0 EndX=52 EndY=37 EndZ=0
    g4: LineSegment StartX=52 StartY=37 StartZ=0 EndX=55 EndY=37 EndZ=0
    g5: LineSegment StartX=20 StartY=5 StartZ=0 EndX=20 EndY=-30 EndZ=0
    g6: LineSegment StartX=20 StartY=-30 StartZ=0 EndX=22.5 EndY=-30 EndZ=0
    g7: LineSegment StartX=22.5 StartY=-30 StartZ=0 EndX=22.5 EndY=0 EndZ=0
    g8: LineSegment StartX=22.5 StartY=0 StartZ=0 EndX=55 EndY=0 EndZ=0
  constraints (26):
    c: PointOnObject(g0,g-1)
    c: Vertical(g0)
    c: PointOnObject(g1,g-1)
    c: Vertical(g1)
    c: Coincident(g1,g2)
    c: Coincident(g2,g0)
    c: DistanceX(g-1,g0) = 20
    c: DistanceY(g0,g0) = 5
    c: Coincident(g0,g3)
    c: Coincident(g3,g4)
    c: Coincident(g4,g1)
    c: Horizontal(g4)
    c: DistanceX(g3,g1) = 3
    c: DistanceX(g2,g2) = 35
    c: Angle(g2,g3) = 0.785398
    c: Coincident(g5,g3)
    c: Vertical(g5)
    c: Coincident(g5,g6)
    c: Horizontal(g6)
    c: Coincident(g6,g7)
    c: PointOnObject(g7,g2)
    c: Vertical(g7)
    c: Coincident(g7,g8)
    c: Coincident(g8,g1)
    c: DistanceX(g-1,g6) = 22.5
    c: DistanceY(g7,g7) = 30
FEATURE [PartDesign::Revolution] Revolution
  Angle = 360
  Axis = (0,2e-16,1)
  Base = (0,0,0)
  Placement = pos=(0,0,0) rot=(1,0,0;1.5708rad)
  Profile = -> Sketch
  ReferenceAxis = -> Sketch [V_Axis]
  Reversed = true
FEATURE [PartDesign::Plane] DatumPlane
  Length = 145.71
  MapMode = 5
  Placement = pos=(0,0,0) rot=(0.57735,0.57735,0.57735;2.0944rad)
  ResizeMode = 0
  Support = -> [YZ_Plane]
  Width = 85.4666
FEATURE [Sketcher::SketchObject] Sketch002
  FullyConstrained = true
  MapMode = 5
  Placement = pos=(0,0,0) rot=(0.57735,0.57735,0.57735;2.0944rad)
  Support = -> [DatumPlane]
  sketch-geometry (4):
    g0: LineSegment StartX=53 StartY=0.1 StartZ=0 EndX=62 EndY=9.55 EndZ=0
    g1: LineSegment StartX=62 StartY=9.55 StartZ=0 EndX=62 EndY=17.55 EndZ=0
    g2: LineSegment StartX=62 StartY=17.55 StartZ=0 EndX=53 EndY=27 EndZ=0
    g3: LineSegment StartX=53 StartY=27 StartZ=0 EndX=53 EndY=0.1 EndZ=0
  constraints (13):
    c: Coincident(g0,g1)
    c: Vertical(g1)
    c: Coincident(g1,g2)
    c: Coincident(g2,g3)
    c: Coincident(g3,g0)
    c: Vertical(g3)
    c: Equal(g2,g0)
    c: DistanceX(g-1,g0) = 53
    c: DistanceX(g-1,g0) = 62
    c: DistanceY(g1,g1) = 8
    c: DistanceY(g-1,g2) = 27
    c: DistanceY(g-1,g0) = 0.1
    c: Angle(g3,g2) = 0.761013
FEATURE [PartDesign::Pad] Pad
  BaseFeature = -> Revolution
  Direction = (1,1,1)
  Length = 12
  Length2 = 100
  Midplane = true
  Placement = pos=(0,0,0) rot=(1,0,0;1.5708rad)
  Profile = -> Sketch002
  Type = 0
FEATURE [Sketcher::SketchObject] Sketch003
  FullyConstrained = true
  MapMode = 5
  Support = -> [XY_Plane]
  sketch-geometry (7):
    g0: LineSegment StartX=0 StartY=0 StartZ=0 EndX=3.5e-15 EndY=57.51 EndZ=0
    g1: LineSegment StartX=-4 StartY=60.01 StartZ=0 EndX=4 EndY=60.01 EndZ=0
    g2: LineSegment StartX=4 StartY=60.01 StartZ=0 EndX=4 EndY=55.01 EndZ=0
    g3: LineSegment StartX=4 StartY=55.01 StartZ=0 EndX=-4 EndY=55.01 EndZ=0
    g4: LineSegment StartX=-4 StartY=55.01 StartZ=0 EndX=-4 EndY=60.01 EndZ=0
    g5: LineSegment StartX=4 StartY=60.01 StartZ=0 EndX=-4 EndY=55.01 EndZ=0
    g6: LineSegment StartX=-4 StartY=60.01 StartZ=0 EndX=4 EndY=55.01 EndZ=0
  constraints (19):
    c: Coincident(g0,g-1)
    c: Coincident(g1,g2)
    c: Coincident(g2,g3)
    c: Coincident(g3,g4)
    c: Coincident(g4,g1)
    c: Coincident(g5,g1)
    c: Coincident(g5,g3)
    c: Coincident(g6,g1)
    c: Coincident(g6,g2)
    c: PointOnObject(g0,g5)
    c: PointOnObject(g0,g6)
    c: Angle(g-1,g0) = 1.5708
    c: Equal(g6,g5)
    c: Parallel(g2,g0)
    c: Perpendicular(g2,g3)
    c: Perpendicular(g4,g3)
    c: Distance(g1) = 8
    c: Distance(g0) = 57.51
    c: Distance(g2) = 5
FEATURE [PartDesign::Pocket] Pocket
  BaseFeature = -> Pad
  Length = 5
  Length2 = 100
  Placement = pos=(0,0,0) rot=(1,0,0;1.5708rad)
  Profile = -> Sketch003
  Reversed = true
  Type = 1
FEATURE [PartDesign::PolarPattern] PolarPattern001
  Angle = 360
  Axis = -> Z_Axis
  BaseFeature = -> Pocket
  Occurrences = 2
  Originals = -> [Pad,Pocket]
  Placement = pos=(0,0,0) rot=(1,0,0;1.5708rad)
FEATURE [PartDesign::Plane] DatumPlane001
  AttachmentOffset = pos=(0,0,0) rot=(0,1,0;1.0472rad)
  Length = 186.237
  MapMode = 5
  Placement = pos=(0,0,0) rot=(0.774597,0.447214,0.447214;1.82348rad)
  ResizeMode = 0
  Support = -> [XZ_Plane]
  Width = 88.0411
FEATURE [Sketcher::SketchObject] Sketch004
  FullyConstrained = true
  MapMode = 5
  Placement = pos=(0,0,0) rot=(0.774597,0.447214,0.447214;1.82348rad)
  Support = -> [DatumPlane001]
  sketch-geometry (4):
    g0: LineSegment StartX=52 StartY=0 StartZ=0 EndX=70 EndY=0 EndZ=0
    g1: LineSegment StartX=70 StartY=0 StartZ=0 EndX=70 EndY=2 EndZ=0
    g2: LineSegment StartX=70 StartY=2 StartZ=0 EndX=52 EndY=20 EndZ=0
    g3: LineSegment StartX=52 StartY=20 StartZ=0 EndX=52 EndY=0 EndZ=0
  constraints (12):
    c: PointOnObject(g0,g-1)
    c: PointOnObject(g0,g-1)
    c: Coincident(g0,g1)
    c: Vertical(g1)
    c: Coincident(g1,g2)
    c: Coincident(g2,g3)
    c: Coincident(g3,g0)
    c: Vertical(g3)
    c: DistanceY(g1,g1) = 2
    c: DistanceX(g-1,g0) = 52
    c: Angle(g2,g0) = 0.785398
    c: DistanceX(g-1,g0) = 70
FEATURE [PartDesign::Pad] Pad001
  BaseFeature = -> PolarPattern001
  Direction = (1,1,1)
  Length = 12
  Length2 = 100
  Midplane = true
  Placement = pos=(0,0,0) rot=(1,0,0;1.5708rad)
  Profile = -> Sketch004
  Type = 0
FEATURE [Sketcher::SketchObject] Sketch005
  AttachmentOffset = pos=(0,0,2) rot=(0,0,1;0rad)
  FullyConstrained = true
  MapMode = 5
  Placement = pos=(0,0,2) rot=(0,0,1;0rad)
  Support = -> [XY_Plane]
  sketch-geometry (5):
    g0: LineSegment StartX=0 StartY=0 StartZ=0 EndX=35.5 EndY=61.4878 EndZ=0
    g1: LineSegment StartX=32.0359 StartY=63.4878 StartZ=0 EndX=38.9641 EndY=59.4878 EndZ=0
    g2: LineSegment StartX=38.9641 StartY=59.4878 StartZ=0 EndX=31.0141 EndY=45.718 EndZ=0
    g3: LineSegment StartX=31.0141 StartY=45.718 StartZ=0 EndX=24.0859 EndY=49.718 EndZ=0
    g4: LineSegment StartX=24.0859 StartY=49.718 StartZ=0 EndX=32.0359 EndY=63.4878 EndZ=0
  constraints (13):
    c: Coincident(g0,g-1)
    c: Coincident(g1,g2)
    c: Coincident(g2,g3)
    c: Coincident(g3,g4)
    c: Coincident(g4,g1)
    c: PointOnObject(g0,g1)
    c: Symmetric(g1,g1,g0)
    c: Symmetric(g2,g3,g0)
    c: Equal(g3,g1)
    c: Angle(g0,g-2) = 0.523599
    c: Distance(g1) = 8
    c: Distance(g-1,g0) = 71
    c: Distance(g-1,g3) = 55.1
FEATURE [PartDesign::Pocket] Pocket001
  BaseFeature = -> Pad001
  Length = 5
  Length2 = 100
  Placement = pos=(0,0,0) rot=(1,0,0;1.5708rad)
  Profile = -> Sketch005
  Reversed = true
  Type = 1
FEATURE [Sketcher::SketchObject] Sketch006
  FullyConstrained = true
  MapMode = 5
  Support = -> [XY_Plane]
  sketch-geometry (2):
    g0: LineSegment StartX=0 StartY=0 StartZ=0 EndX=32.5 EndY=56.2917 EndZ=0
    g1: Circle CenterX=32.5 CenterY=56.2917 CenterZ=0 NormalX=0 NormalY=0 NormalZ=1 AngleXU=0 Radius=2.15
  constraints (5):
    c: Coincident(g0,g-1)
    c: Coincident(g1,g0)
    c: Distance(g0) = 65
    c: Angle(g0,g-2) = 0.523599
    c: Diameter(g1) = 4.3
FEATURE [PartDesign::Pocket] Pocket002
  BaseFeature = -> Pocket001
  Length = 5
  Length2 = 100
  Placement = pos=(0,0,0) rot=(1,0,0;1.5708rad)
  Profile = -> Sketch006
  Reversed = true
  Type = 1
FEATURE [PartDesign::PolarPattern] PolarPattern002
  Angle = 60
  Axis = -> Z_Axis
  BaseFeature = -> Pocket002
  Occurrences = 2
  Originals = -> [Pad001,Pocket001,Pocket002]
  Placement = pos=(0,0,0) rot=(1,0,0;1.5708rad)
FEATURE [PartDesign::PolarPattern] PolarPattern003
  Angle = 360
  Axis = -> Z_Axis
  BaseFeature = -> PolarPattern002
  Occurrences = 2
  Originals = -> [Pad001,Pocket001,Pocket002]
  Placement = pos=(0,0,0) rot=(1,0,0;1.5708rad)
FEATURE [PartDesign::PolarPattern] PolarPattern004
  Angle = 240
  Axis = -> Z_Axis
  BaseFeature = -> PolarPattern003
  Occurrences = 2
  Originals = -> [Pad001,Pocket001,Pocket002]
  Placement = pos=(0,0,0) rot=(1,0,0;1.5708rad)
FEATURE [PartDesign::Fillet] Fillet
  Base = -> PolarPattern004 [Edge1]
  BaseFeature = -> PolarPattern004
  Placement = pos=(0,0,0) rot=(1,0,0;1.5708rad)
  Radius = 10
  SupportTransform = false
FEATURE [PartDesign::Body] Body
  Group = -> [Sketch,Revolution,DatumPlane,Sketch002,Pad,Sketch003,Pocket,PolarPattern001,DatumPlane001,Sketch004,Pad001,Sketch005,Pocket001,Sketch006,Pocket002,PolarPattern002,PolarPattern003,PolarPattern004,Fillet]
  Origin = -> Origin
  Tip = -> Fillet
